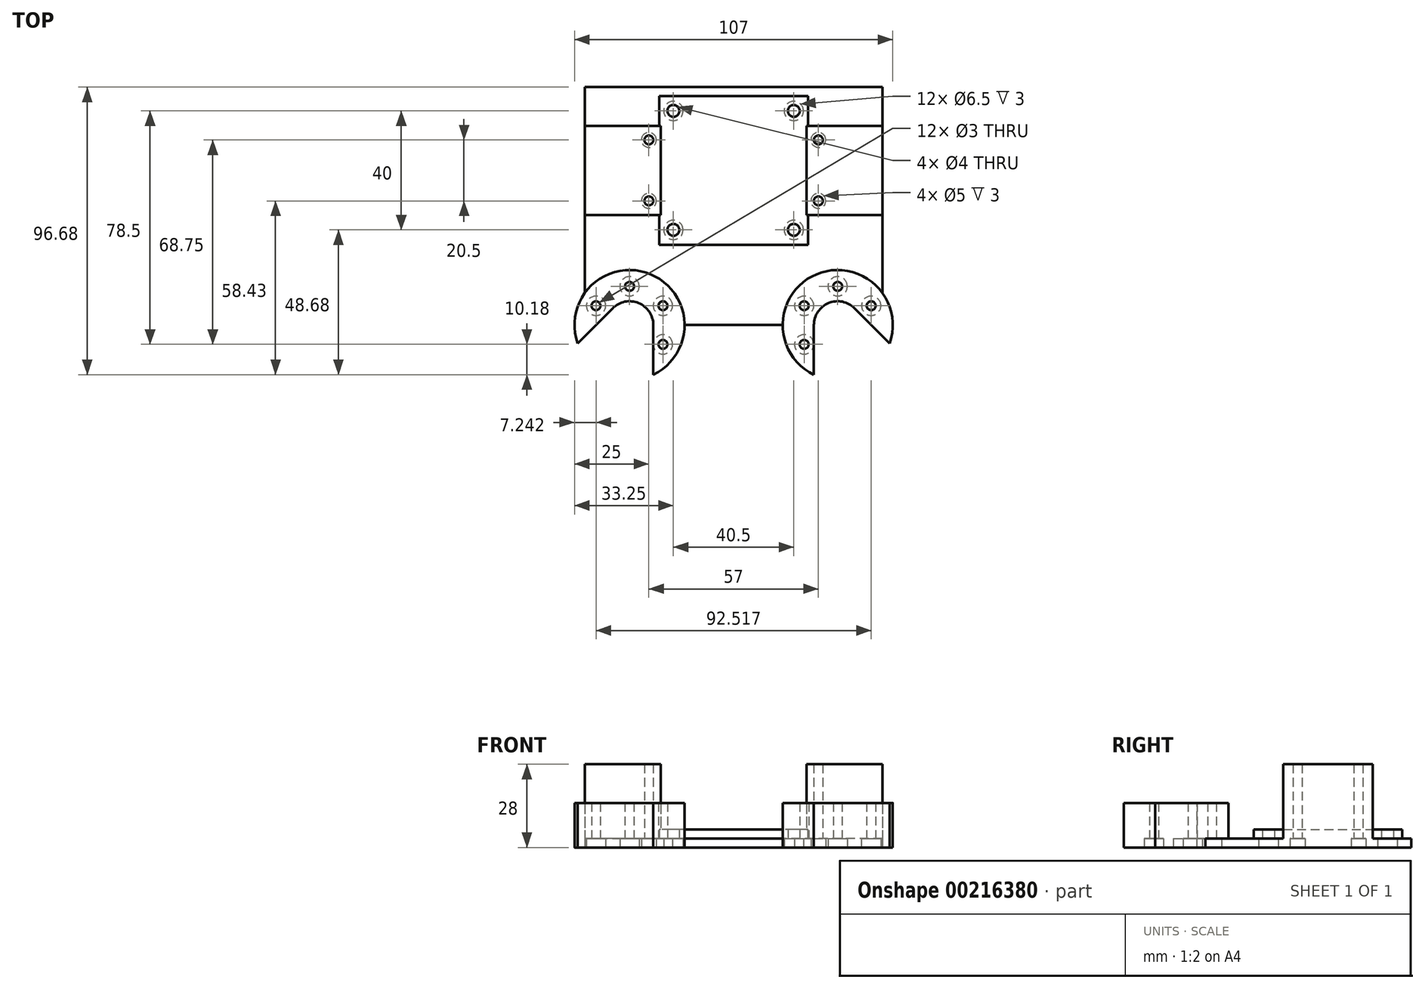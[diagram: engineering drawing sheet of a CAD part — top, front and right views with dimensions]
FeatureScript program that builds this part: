
annotation { "Feature Type Name" : "Feature", "Feature Type Description" : "" }
export const myFeature = defineFeature(function(context is Context, id is Id, definition is map)
    precondition{}
    {
        {
            var Q0;
            Q0=qCreatedBy(makeId("Top.planeOp"),FACE);
            var sketch = newSketch(context, id + "F0", { "sketchPlane" : qUnion([Q0])});
            skLineSegment(sketch, "E0.bottom", {"start": v(50, -40) * mm, "end": v(-50, -40) * mm});
            skLineSegment(sketch, "E0.top", {"start": v(50, 40) * mm, "end": v(-50, 40) * mm});
            skLineSegment(sketch, "E0.left", {"start": v(50, -40) * mm, "end": v(50, 40) * mm});
            skLineSegment(sketch, "E0.right", {"start": v(-50, -40) * mm, "end": v(-50, 40) * mm});
            skPoint(sketch, "E0.middle", {"position": v(0, 0) * mm});
            skSolve(sketch);
        }
        {
            var Q0;
            Q0 = qSketchRegion(id + "F0", true);
            extrude(context, id + "F1", {"entities" : qUnion([Q0]), "depth" : 3 * mm});
        }
        {
            var Q0;
            Q0=makeQuery(id+"F1.opExtrude","CAP_FACE",FACE,{"disambiguationData":[OSD([sQuery(id+"F0.wireOp",EDGE,"E0.bottom"),sQuery(id+"F0.wireOp",EDGE,"E0.top"),sQuery(id+"F0.wireOp",EDGE,"E0.left"),sQuery(id+"F0.wireOp",EDGE,"E0.right")])],"isStart":true});
            var sketch = newSketch(context, id + "F2", { "sketchPlane" : qUnion([Q0])});
            skPoint(sketch, "E1", {"position": v(-20.25, 8) * mm});
            skPoint(sketch, "E2", {"position": v(20.25, 8) * mm});
            skPoint(sketch, "E3", {"position": v(-46.26, 46.5) * mm});
            skPoint(sketch, "E4.1.0", {"position": v(-46.26, 33.5) * mm});
            skPoint(sketch, "E4.2.0", {"position": v(-35, 27) * mm});
            skPoint(sketch, "E4.3.0", {"position": v(-23.74, 33.5) * mm});
            skPoint(sketch, "E4.4.0", {"position": v(-23.74, 46.5) * mm});
            skPoint(sketch, "E4.5.0", {"position": v(-35, 53) * mm});
            skPoint(sketch, "E4.center", {"position": v(-35, 40) * mm});
            skPoint(sketch, "E5.MirrorP", {"position": v(23.74, 33.5) * mm});
            skPoint(sketch, "E6.MirrorP", {"position": v(35, 27) * mm});
            skPoint(sketch, "E7.MirrorP", {"position": v(46.26, 33.5) * mm});
            skPoint(sketch, "E8.MirrorP", {"position": v(46.26, 46.5) * mm});
            skPoint(sketch, "E9.MirrorP", {"position": v(35, 53) * mm});
            skPoint(sketch, "E10.MirrorP", {"position": v(23.74, 46.5) * mm});
            skPoint(sketch, "E11.MirrorP", {"position": v(35, 40) * mm});
            skCircle(sketch, "E12", {"center": v(-35, 40) * mm, "radius": 18.5 * mm});
            skCircle(sketch, "E13", {"center": v(35, 40) * mm, "radius": 18.5 * mm});
            skPoint(sketch, "E14.1.0.0", {"position": v(-20.25, 48) * mm});
            skPoint(sketch, "E14.1.0.1", {"position": v(20.25, 48) * mm});
            skLineSegment(sketch, "E14.direction1", {"start": v(-20.25, 8) * mm, "end": v(-20.25, 48) * mm, "construction": true});
            skPoint(sketch, "E15", {"position": v(-20.25, -32) * mm});
            skPoint(sketch, "E16", {"position": v(20.25, -32) * mm});
            skPoint(sketch, "E17", {"position": v(-28.5, -22.25) * mm});
            skPoint(sketch, "E18", {"position": v(-28.5, -1.75) * mm});
            skPoint(sketch, "E19", {"position": v(28.5, -22.25) * mm});
            skPoint(sketch, "E20", {"position": v(28.5, -1.75) * mm});
            skLineSegment(sketch, "E21", {"start": v(-20.25, -32) * mm, "end": v(-20.25, 8) * mm, "construction": true});
            skLineSegment(sketch, "E22", {"start": v(20.25, -32) * mm, "end": v(20.25, 8) * mm, "construction": true});
            skLineSegment(sketch, "E23", {"start": v(-20.25, -12) * mm, "end": v(20.25, -12) * mm, "construction": true});
            skSolve(sketch);
        }
        {
            var Q0;
            Q0=qCreatedBy(makeId("Top.planeOp"),FACE);
            var sketch = newSketch(context, id + "F3", { "sketchPlane" : qUnion([Q0])});
            skLineSegment(sketch, "E24.bottom", {"start": v(-24.5, -3) * mm, "end": v(-50, -3) * mm});
            skLineSegment(sketch, "E24.top", {"start": v(-24.5, 27) * mm, "end": v(-50, 27) * mm});
            skLineSegment(sketch, "E24.left", {"start": v(-24.5, -3) * mm, "end": v(-24.5, 27) * mm});
            skLineSegment(sketch, "E24.right", {"start": v(-50, -3) * mm, "end": v(-50, 27) * mm});
            skPoint(sketch, "E24.middle", {"position": v(-37.25, 12) * mm});
            skLineSegment(sketch, "E25.MirrorCS", {"start": v(24.5, -3) * mm, "end": v(24.5, 27) * mm});
            skLineSegment(sketch, "E26.MirrorCS", {"start": v(24.5, 27) * mm, "end": v(50, 27) * mm});
            skLineSegment(sketch, "E27.MirrorCS", {"start": v(50, -3) * mm, "end": v(50, 27) * mm});
            skLineSegment(sketch, "E28.MirrorCS", {"start": v(24.5, -3) * mm, "end": v(50, -3) * mm});
            skSolve(sketch);
        }
        {
            var Q0;
            Q0=makeQuery(id+"F2.imprint","IMPRINT",FACE,{"disambiguationData":[TD([[makeQuery(id+"F2.imprint","IMPRINT",EDGE,{"derivedFrom":sQuery(id+"F2.wireOp",EDGE,"E12")}),1.0]])]});
            var Q1;
            Q1=makeQuery(id+"F2.imprint","IMPRINT",FACE,{"disambiguationData":[TD([[makeQuery(id+"F2.imprint","IMPRINT",EDGE,{"derivedFrom":sQuery(id+"F2.wireOp",EDGE,"E13")}),1.0]])]});
            extrude(context, id + "F4", {"entities" : qUnion([Q0, Q1]), "operationType" : NewBodyOperationType.ADD, "oppositeDirection" : true, "depth" : 15 * mm});
        }
        {
            var Q0;
            Q0=makeQuery(id+"F4.opExtrude","CAP_FACE",FACE,{"disambiguationData":[OSD([sQuery(id+"F2.wireOp",EDGE,"E12")])],"isStart":false});
            var sketch = newSketch(context, id + "F5", { "sketchPlane" : qUnion([Q0])});
            skArc(sketch, "E29", {"start": v(-27, -40) * mm, "mid": v(-31.94, -32.6) * mm, "end": v(-40.66, -34.34) * mm});
            skLineSegment(sketch, "E30", {"start": v(-27, -40) * mm, "end": v(-27, -56.68) * mm});
            skLineSegment(sketch, "E31", {"start": v(-40.66, -34.34) * mm, "end": v(-52.45, -46.14) * mm});
            skArc(sketch, "E32", {"start": v(-52.45, -46.14) * mm, "mid": v(-42.08, -57.1) * mm, "end": v(-27, -56.68) * mm});
            skLineSegment(sketch, "E33.MirrorCS", {"start": v(27, -40) * mm, "end": v(27, -56.68) * mm});
            skArc(sketch, "E34.MirrorCS", {"start": v(27, -40) * mm, "mid": v(31.94, -32.6) * mm, "end": v(40.66, -34.34) * mm});
            skLineSegment(sketch, "E35.MirrorCS", {"start": v(40.66, -34.34) * mm, "end": v(52.45, -46.14) * mm});
            skArc(sketch, "E36.MirrorCS", {"start": v(52.45, -46.14) * mm, "mid": v(42.08, -57.1) * mm, "end": v(27, -56.68) * mm});
            skSolve(sketch);
        }
        {
            var Q0;
            Q0 = qSketchRegion(id + "F5", true);
            extrude(context, id + "F6", {"entities" : qUnion([Q0]), "operationType" : NewBodyOperationType.REMOVE, "endBound" : BoundingType.THROUGH_ALL, "oppositeDirection" : true, "depth" : 12 * mm});
        }
        {
            var Q0;
            Q0 = qSketchRegion(id + "F3", true);
            extrude(context, id + "F7", {"entities" : qUnion([Q0]), "operationType" : NewBodyOperationType.ADD, "depth" : 28 * mm});
        }
        {
            var Q0;
            Q0=qCreatedBy(makeId("Top.planeOp"),FACE);
            var sketch = newSketch(context, id + "F8", { "sketchPlane" : qUnion([Q0])});
            skLineSegment(sketch, "E37.bottom", {"start": v(25, -13) * mm, "end": v(-25, -13) * mm});
            skLineSegment(sketch, "E37.top", {"start": v(25, 37) * mm, "end": v(-25, 37) * mm});
            skLineSegment(sketch, "E37.left", {"start": v(25, -13) * mm, "end": v(25, 37) * mm});
            skLineSegment(sketch, "E37.right", {"start": v(-25, -13) * mm, "end": v(-25, 37) * mm});
            skPoint(sketch, "E37.middle", {"position": v(0, 12) * mm});
            skSolve(sketch);
        }
        {
            var Q0;
            Q0 = qSketchRegion(id + "F8", true);
            extrude(context, id + "F9", {"entities" : qUnion([Q0]), "operationType" : NewBodyOperationType.ADD, "depth" : 6 * mm});
        }
        {
            var Q0;
            Q0=sQuery(id+"F2.wireOp",VERTEX,"E1");
            var Q1;
            Q1=sQuery(id+"F2.wireOp",VERTEX,"E2");
            var Q2;
            Q2=sQuery(id+"F2.wireOp",VERTEX,"E15");
            var Q3;
            Q3=sQuery(id+"F2.wireOp",VERTEX,"E16");
            var Q4;
            Q4=makeQuery(id+"F1.opExtrude","SWEPT_BODY",BODY,{"disambiguationData":[OSD([sQuery(id+"F0.wireOp",EDGE,"E0.bottom"),sQuery(id+"F0.wireOp",EDGE,"E0.top"),sQuery(id+"F0.wireOp",EDGE,"E0.left"),sQuery(id+"F0.wireOp",EDGE,"E0.right")])]});
            hole(context, id + "F10", {"style" : HoleStyle.C_BORE, "endStyle" : HoleEndStyle.THROUGH, "holeDiameter" : 4 * mm, "cBoreDiameter" : 6.5 * mm, "cBoreDepth" : 3 * mm, "tappedDepth" : 12 * mm, "tapClearance" : 3, "locations" : qUnion([Q0, Q1, Q2, Q3]), "scope" : qUnion([Q4])});
        }
        {
            var Q0;
            Q0=sQuery(id+"F2.wireOp",VERTEX,"E4.1.0");
            var Q1;
            Q1=sQuery(id+"F2.wireOp",VERTEX,"E3");
            var Q2;
            Q2=sQuery(id+"F2.wireOp",VERTEX,"E4.4.0");
            var Q3;
            Q3=sQuery(id+"F2.wireOp",VERTEX,"E4.3.0");
            var Q4;
            Q4=sQuery(id+"F2.wireOp",VERTEX,"E4.2.0");
            var Q5;
            Q5=sQuery(id+"F2.wireOp",VERTEX,"E10.MirrorP");
            var Q6;
            Q6=sQuery(id+"F2.wireOp",VERTEX,"E8.MirrorP");
            var Q7;
            Q7=sQuery(id+"F2.wireOp",VERTEX,"E7.MirrorP");
            var Q8;
            Q8=sQuery(id+"F2.wireOp",VERTEX,"E6.MirrorP");
            var Q9;
            Q9=sQuery(id+"F2.wireOp",VERTEX,"E5.MirrorP");
            var Q10;
            Q10=makeQuery(id+"F1.opExtrude","SWEPT_BODY",BODY,{"disambiguationData":[OSD([sQuery(id+"F0.wireOp",EDGE,"E0.bottom"),sQuery(id+"F0.wireOp",EDGE,"E0.top"),sQuery(id+"F0.wireOp",EDGE,"E0.left"),sQuery(id+"F0.wireOp",EDGE,"E0.right")])]});
            hole(context, id + "F11", {"style" : HoleStyle.C_BORE, "endStyle" : HoleEndStyle.THROUGH, "holeDiameter" : 3 * mm, "cBoreDiameter" : 6.5 * mm, "cBoreDepth" : 3 * mm, "tappedDepth" : 12 * mm, "tapClearance" : 3, "locations" : qUnion([Q0, Q1, Q2, Q3, Q4, Q5, Q6, Q7, Q8, Q9]), "scope" : qUnion([Q10])});
        }
        {
            var Q0;
            Q0=sQuery(id+"F2.wireOp",VERTEX,"E17");
            var Q1;
            Q1=sQuery(id+"F2.wireOp",VERTEX,"E18");
            var Q2;
            Q2=sQuery(id+"F2.wireOp",VERTEX,"E19");
            var Q3;
            Q3=sQuery(id+"F2.wireOp",VERTEX,"E20");
            var Q4;
            Q4=makeQuery(id+"F1.opExtrude","SWEPT_BODY",BODY,{"disambiguationData":[OSD([sQuery(id+"F0.wireOp",EDGE,"E0.bottom"),sQuery(id+"F0.wireOp",EDGE,"E0.top"),sQuery(id+"F0.wireOp",EDGE,"E0.left"),sQuery(id+"F0.wireOp",EDGE,"E0.right")])]});
            hole(context, id + "F12", {"style" : HoleStyle.C_BORE, "endStyle" : HoleEndStyle.THROUGH, "holeDiameter" : 3 * mm, "cBoreDiameter" : 5 * mm, "cBoreDepth" : 3 * mm, "tappedDepth" : 12 * mm, "tapClearance" : 3, "locations" : qUnion([Q0, Q1, Q2, Q3]), "scope" : qUnion([Q4])});
        }
    });
